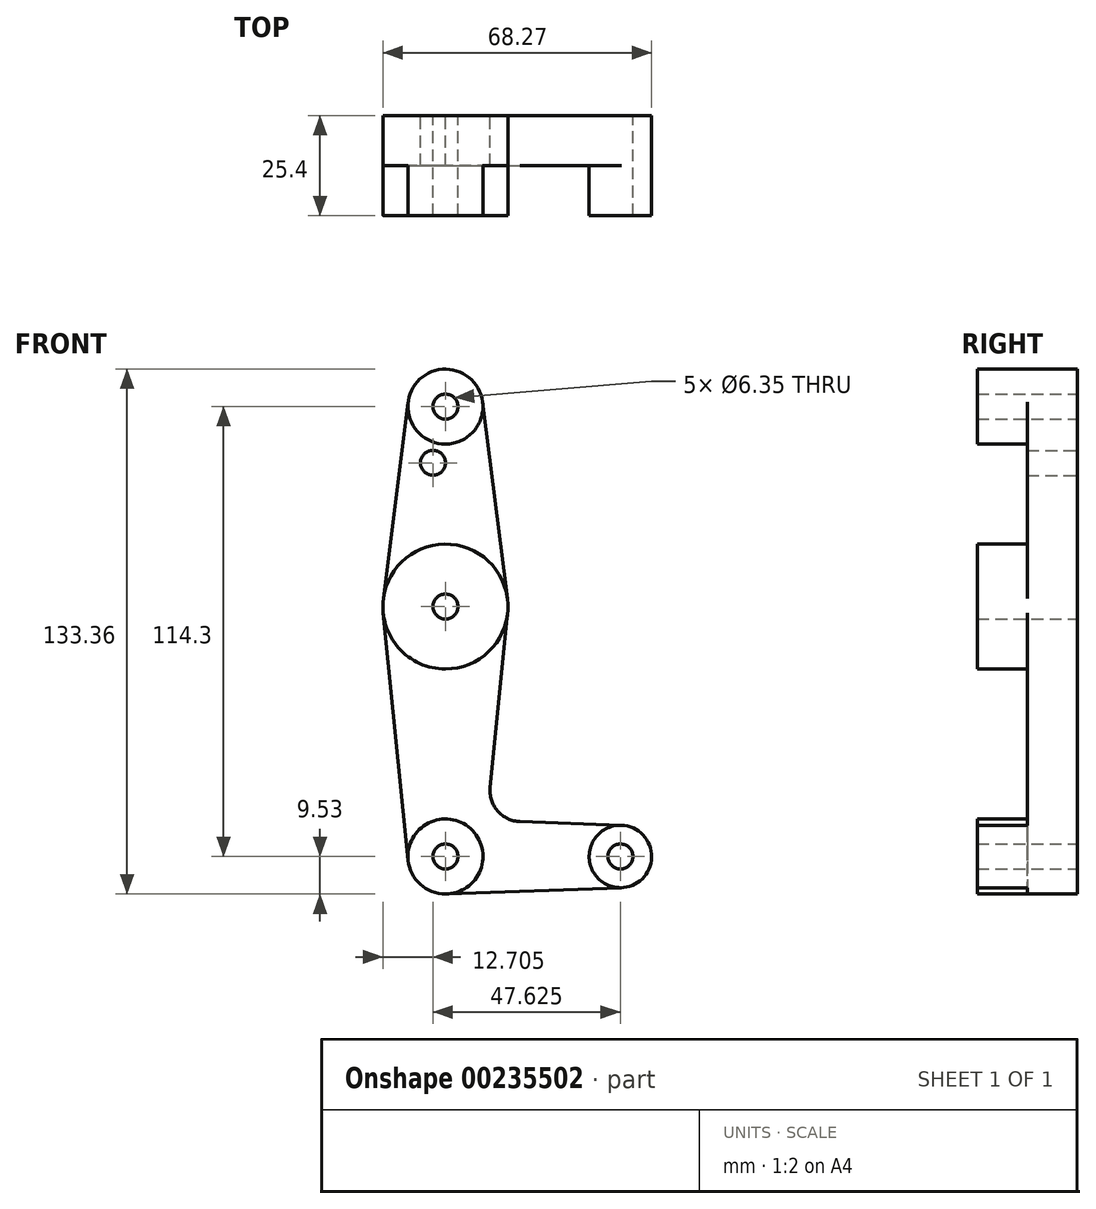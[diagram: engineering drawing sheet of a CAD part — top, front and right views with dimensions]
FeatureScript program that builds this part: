
annotation { "Feature Type Name" : "Feature", "Feature Type Description" : "" }
export const myFeature = defineFeature(function(context is Context, id is Id, definition is map)
    precondition{}
    {
        {
            var Q0;
            Q0=qCreatedBy(makeId("Front.planeOp"),FACE);
            var sketch = newSketch(context, id + "F0", { "sketchPlane" : qUnion([Q0])});
            skCircle(sketch, "E0", {"center": v(0, 0) * mm, "radius": 15.88 * mm});
            skCircle(sketch, "E1", {"center": v(0, 50.8) * mm, "radius": 9.53 * mm});
            skCircle(sketch, "E2", {"center": v(0, -63.5) * mm, "radius": 9.53 * mm});
            skLineSegment(sketch, "E3", {"start": v(-9.45, 52) * mm, "end": v(-15.75, 1.98) * mm});
            skLineSegment(sketch, "E4", {"start": v(9.45, 52) * mm, "end": v(15.75, 1.98) * mm});
            skLineSegment(sketch, "E5", {"start": v(-9.48, -64.45) * mm, "end": v(-15.8, -1.59) * mm});
            skCircle(sketch, "E6", {"center": v(0, 50.8) * mm, "radius": 3.18 * mm});
            skCircle(sketch, "E7", {"center": v(0, 0) * mm, "radius": 3.18 * mm});
            skCircle(sketch, "E8", {"center": v(0, -63.5) * mm, "radius": 3.18 * mm});
            skCircle(sketch, "E9", {"center": v(44.45, -63.5) * mm, "radius": 7.94 * mm});
            skLineSegment(sketch, "E10", {"start": v(15.8, -1.59) * mm, "end": v(11.34, -45.9) * mm});
            skLineSegment(sketch, "E11", {"start": v(0.34, -73.02) * mm, "end": v(44.73, -71.43) * mm});
            skLineSegment(sketch, "E12", {"start": v(44.73, -55.57) * mm, "end": v(18.97, -54.65) * mm});
            skArc(sketch, "E13.filletArc", {"start": v(11.34, -45.9) * mm, "mid": v(13.26, -51.93) * mm, "end": v(18.97, -54.65) * mm});
            skCircle(sketch, "E14", {"center": v(44.45, -63.5) * mm, "radius": 3.18 * mm});
            skCircle(sketch, "E15", {"center": v(-3.18, 36.53) * mm, "radius": 3.18 * mm});
            skSolve(sketch);
        }
        {
            var Q0;
            Q0=makeQuery(id+"F0.imprint","IMPRINT",FACE,{"disambiguationData":[TD([[makeQuery(id+"F0.imprint","IMPRINT",EDGE,{"derivedFrom":sQuery(id+"F0.wireOp",EDGE,"E6")}),-1.0]])]});
            var Q1;
            Q1=makeQuery(id+"F0.imprint","IMPRINT",FACE,{"disambiguationData":[TD([[makeQuery(id+"F0.imprint","IMPRINT",EDGE,{"derivedFrom":sQuery(id+"F0.wireOp",EDGE,"E7")}),-1.0]])]});
            var Q2;
            Q2=makeQuery(id+"F0.imprint","IMPRINT",FACE,{"disambiguationData":[TD([[makeQuery(id+"F0.imprint","IMPRINT",EDGE,{"derivedFrom":sQuery(id+"F0.wireOp",EDGE,"E8")}),-1.0]])]});
            var Q3;
            Q3=makeQuery(id+"F0.imprint","IMPRINT",FACE,{"disambiguationData":[TD([[makeQuery(id+"F0.imprint","IMPRINT",EDGE,{"derivedFrom":sQuery(id+"F0.wireOp",EDGE,"E14")}),-1.0]])]});
            extrude(context, id + "F1", {"entities" : qUnion([Q0, Q1, Q2, Q3]), "depth" : 25.4 * mm});
        }
        {
            var Q0;
            {var subQ1=sQuery(id+"F0.wireOp",EDGE,"E3");Q0=makeQuery(id+"F0.imprint","IMPRINT",FACE,{"disambiguationData":[TD([[makeQuery(id+"F0.imprint","IMPRINT",EDGE,{"derivedFrom":subQ1}),1.0]])]});}
            var Q1;
            {var subQ3=sQuery(id+"F0.wireOp",EDGE,"E5");Q1=makeQuery(id+"F0.imprint","IMPRINT",FACE,{"disambiguationData":[TD([[makeQuery(id+"F0.imprint","IMPRINT",EDGE,{"derivedFrom":subQ3}),-1.0]])]});}
            extrude(context, id + "F2", {"entities" : qUnion([Q0, Q1]), "operationType" : NewBodyOperationType.ADD, "depth" : 12.7 * mm});
        }
    });
